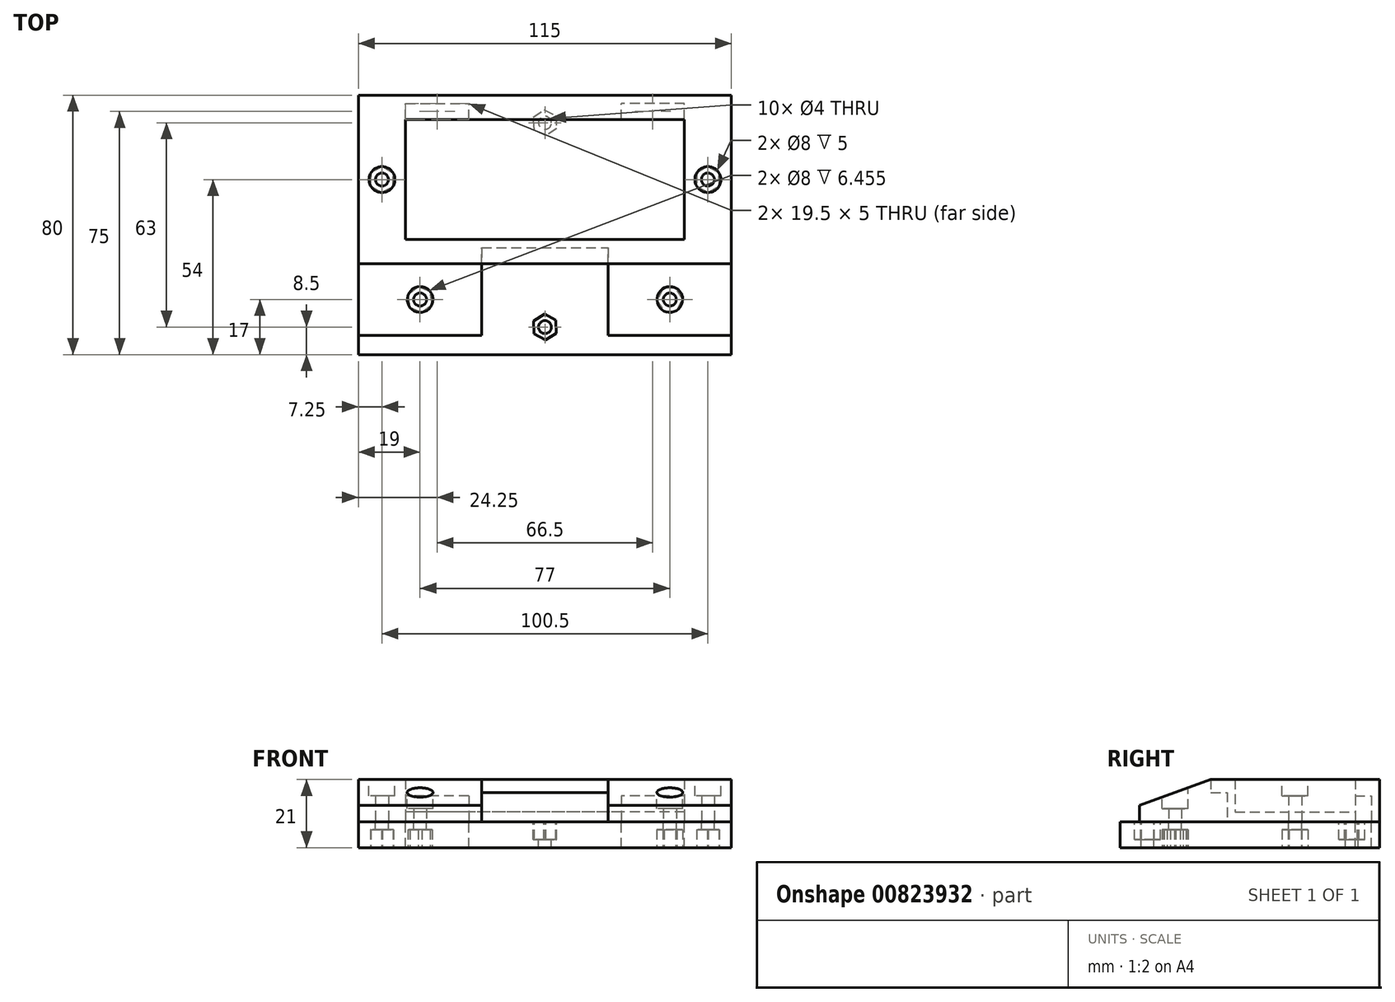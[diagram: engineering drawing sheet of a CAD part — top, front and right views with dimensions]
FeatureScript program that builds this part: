
annotation { "Feature Type Name" : "Feature", "Feature Type Description" : "" }
export const myFeature = defineFeature(function(context is Context, id is Id, definition is map)
    precondition{}
    {
        {
            var Q0;
            Q0=qCreatedBy(makeId("Top.planeOp"),FACE);
            var sketch = newSketch(context, id + "F0", { "sketchPlane" : qUnion([Q0])});
            skLineSegment(sketch, "E0.bottom", {"start": v(1460.5, -1028.53) * mm, "end": v(-1460.5, -1028.53) * mm});
            skLineSegment(sketch, "E0.top", {"start": v(1460.5, 1028.53) * mm, "end": v(-1460.5, 1028.53) * mm});
            skLineSegment(sketch, "E0.left", {"start": v(1460.5, -1028.53) * mm, "end": v(1460.5, 1028.53) * mm});
            skLineSegment(sketch, "E0.right", {"start": v(-1460.5, -1028.53) * mm, "end": v(-1460.5, 1028.53) * mm});
            skPoint(sketch, "E0.middle", {"position": v(0, 0) * mm});
            skLineSegment(sketch, "E1.bottom", {"start": v(57.5, -26) * mm, "end": v(-57.5, -26) * mm});
            skLineSegment(sketch, "E1.top", {"start": v(57.5, 26) * mm, "end": v(-57.5, 26) * mm});
            skLineSegment(sketch, "E1.left", {"start": v(57.5, -26) * mm, "end": v(57.5, 26) * mm});
            skLineSegment(sketch, "E1.right", {"start": v(-57.5, -26) * mm, "end": v(-57.5, 26) * mm});
            skLineSegment(sketch, "E2.bottom", {"start": v(43, -18.5) * mm, "end": v(-43, -18.5) * mm});
            skLineSegment(sketch, "E2.top", {"start": v(43, 18.5) * mm, "end": v(-43, 18.5) * mm});
            skLineSegment(sketch, "E2.left", {"start": v(43, -18.5) * mm, "end": v(43, 18.5) * mm});
            skLineSegment(sketch, "E2.right", {"start": v(-43, -18.5) * mm, "end": v(-43, 18.5) * mm});
            skLineSegment(sketch, "E3.bottom", {"start": v(-57.5, -26) * mm, "end": v(-19.5, -26) * mm});
            skLineSegment(sketch, "E3.top", {"start": v(-57.5, -48) * mm, "end": v(-19.5, -48) * mm});
            skLineSegment(sketch, "E3.left", {"start": v(-57.5, -26) * mm, "end": v(-57.5, -48) * mm});
            skLineSegment(sketch, "E3.right", {"start": v(-19.5, -26) * mm, "end": v(-19.5, -48) * mm});
            skLineSegment(sketch, "E4.bottom", {"start": v(57.5, -26) * mm, "end": v(19.5, -26) * mm});
            skLineSegment(sketch, "E4.top", {"start": v(57.5, -48) * mm, "end": v(19.5, -48) * mm});
            skLineSegment(sketch, "E4.left", {"start": v(57.5, -26) * mm, "end": v(57.5, -48) * mm});
            skLineSegment(sketch, "E4.right", {"start": v(19.5, -26) * mm, "end": v(19.5, -48) * mm});
            skLineSegment(sketch, "E5.bottom", {"start": v(-43, 18.5) * mm, "end": v(-23.5, 18.5) * mm});
            skLineSegment(sketch, "E5.top", {"start": v(-43, 23.5) * mm, "end": v(-23.5, 23.5) * mm});
            skLineSegment(sketch, "E5.left", {"start": v(-43, 18.5) * mm, "end": v(-43, 23.5) * mm});
            skLineSegment(sketch, "E5.right", {"start": v(-23.5, 18.5) * mm, "end": v(-23.5, 23.5) * mm});
            skLineSegment(sketch, "E6.bottom", {"start": v(43, 18.5) * mm, "end": v(23.5, 18.5) * mm});
            skLineSegment(sketch, "E6.top", {"start": v(43, 23.5) * mm, "end": v(23.5, 23.5) * mm});
            skLineSegment(sketch, "E6.left", {"start": v(43, 18.5) * mm, "end": v(43, 23.5) * mm});
            skLineSegment(sketch, "E6.right", {"start": v(23.5, 18.5) * mm, "end": v(23.5, 23.5) * mm});
            skLineSegment(sketch, "E7.bottom", {"start": v(-19.5, -26) * mm, "end": v(19.5, -26) * mm});
            skLineSegment(sketch, "E7.top", {"start": v(-19.5, -21) * mm, "end": v(19.5, -21) * mm});
            skLineSegment(sketch, "E7.left", {"start": v(-19.5, -26) * mm, "end": v(-19.5, -21) * mm});
            skLineSegment(sketch, "E7.right", {"start": v(19.5, -26) * mm, "end": v(19.5, -21) * mm});
            skLineSegment(sketch, "E8", {"start": v(-57.5, -48) * mm, "end": v(-19.5, -26) * mm, "construction": true});
            skLineSegment(sketch, "E9", {"start": v(-57.5, -26) * mm, "end": v(-19.5, -48) * mm, "construction": true});
            skLineSegment(sketch, "E10", {"start": v(19.5, -26) * mm, "end": v(57.5, -48) * mm, "construction": true});
            skLineSegment(sketch, "E11", {"start": v(57.5, -26) * mm, "end": v(19.5, -48) * mm, "construction": true});
            skCircle(sketch, "E12", {"center": v(-38.5, -37) * mm, "radius": 4 * mm});
            skCircle(sketch, "E13", {"center": v(38.5, -37) * mm, "radius": 4 * mm});
            skCircle(sketch, "E14", {"center": v(-38.5, -37) * mm, "radius": 2 * mm});
            skCircle(sketch, "E15", {"center": v(38.5, -37) * mm, "radius": 2 * mm});
            skLineSegment(sketch, "E16", {"start": v(-57.5, 0) * mm, "end": v(-43, 0) * mm, "construction": true});
            skLineSegment(sketch, "E17", {"start": v(-43, 0) * mm, "end": v(43, 0) * mm, "construction": true});
            skLineSegment(sketch, "E18", {"start": v(43, 0) * mm, "end": v(57.5, 0) * mm, "construction": true});
            skPoint(sketch, "E19", {"position": v(-50.25, 0) * mm});
            skPoint(sketch, "E20", {"position": v(50.25, 0) * mm});
            skCircle(sketch, "E21", {"center": v(-50.25, 0) * mm, "radius": 4 * mm});
            skCircle(sketch, "E22", {"center": v(50.25, 0) * mm, "radius": 4 * mm});
            skCircle(sketch, "E23", {"center": v(50.25, 0) * mm, "radius": 2 * mm});
            skCircle(sketch, "E24", {"center": v(-50.25, 0) * mm, "radius": 2 * mm});
            skSolve(sketch);
        }
        {
            var Q0;
            Q0=makeQuery(id+"F0.imprint","IMPRINT",FACE,{"disambiguationData":[TD([[makeQuery(id+"F0.imprint","IMPRINT",EDGE,{"derivedFrom":sQuery(id+"F0.wireOp",EDGE,"E1.top")}),1.0]])]});
            var Q1;
            Q1=makeQuery(id+"F0.imprint","IMPRINT",FACE,{"disambiguationData":[TD([[makeQuery(id+"F0.imprint","IMPRINT",EDGE,{"derivedFrom":sQuery(id+"F0.wireOp",EDGE,"E21")}),1.0]])]});
            var Q2;
            Q2=makeQuery(id+"F0.imprint","IMPRINT",FACE,{"disambiguationData":[TD([[makeQuery(id+"F0.imprint","IMPRINT",EDGE,{"derivedFrom":sQuery(id+"F0.wireOp",EDGE,"E22")}),1.0]])]});
            var Q3;
            Q3=makeQuery(id+"F0.imprint","IMPRINT",FACE,{"disambiguationData":[TD([[makeQuery(id+"F0.imprint","IMPRINT",EDGE,{"derivedFrom":sQuery(id+"F0.wireOp",EDGE,"E5.top")}),-1.0]])]});
            var Q4;
            Q4=makeQuery(id+"F0.imprint","IMPRINT",FACE,{"disambiguationData":[TD([[makeQuery(id+"F0.imprint","IMPRINT",EDGE,{"derivedFrom":sQuery(id+"F0.wireOp",EDGE,"E6.top")}),1.0]])]});
            var Q5;
            Q5=makeQuery(id+"F0.imprint","IMPRINT",FACE,{"disambiguationData":[TD([[makeQuery(id+"F0.imprint","IMPRINT",EDGE,{"derivedFrom":sQuery(id+"F0.wireOp",EDGE,"E7.top")}),-1.0]])]});
            extrude(context, id + "F1", {"entities" : qUnion([Q0, Q1, Q2, Q3, Q4, Q5]), "depth" : 13 * mm, "offsetDistance" : 25 * mm});
        }
        {
            var Q0;
            Q0=makeQuery(id+"F0.imprint","IMPRINT",FACE,{"disambiguationData":[TD([[makeQuery(id+"F0.imprint","IMPRINT",EDGE,{"derivedFrom":sQuery(id+"F0.wireOp",EDGE,"E2.bottom")}),-1.0]])]});
            extrude(context, id + "F2", {"entities" : qUnion([Q0]), "operationType" : NewBodyOperationType.ADD, "depth" : 3 * mm, "offsetDistance" : 25 * mm});
        }
        {
            var Q0;
            Q0=makeQuery(id+"F0.imprint","IMPRINT",FACE,{"disambiguationData":[TD([[makeQuery(id+"F0.imprint","IMPRINT",EDGE,{"derivedFrom":sQuery(id+"F0.wireOp",EDGE,"E5.top")}),-1.0]])]});
            var Q1;
            Q1=makeQuery(id+"F0.imprint","IMPRINT",FACE,{"disambiguationData":[TD([[makeQuery(id+"F0.imprint","IMPRINT",EDGE,{"derivedFrom":sQuery(id+"F0.wireOp",EDGE,"E6.top")}),1.0]])]});
            extrude(context, id + "F3", {"entities" : qUnion([Q0, Q1]), "operationType" : NewBodyOperationType.REMOVE, "oppositeDirection" : true, "depth" : -8 * mm, "offsetDistance" : 25 * mm});
        }
        {
            var Q0;
            Q0=makeQuery(id+"F0.imprint","IMPRINT",FACE,{"disambiguationData":[TD([[makeQuery(id+"F0.imprint","IMPRINT",EDGE,{"derivedFrom":sQuery(id+"F0.wireOp",EDGE,"E3.top")}),1.0]])]});
            var Q1;
            Q1=makeQuery(id+"F0.imprint","IMPRINT",FACE,{"disambiguationData":[TD([[makeQuery(id+"F0.imprint","IMPRINT",EDGE,{"derivedFrom":sQuery(id+"F0.wireOp",EDGE,"E12")}),1.0]])]});
            var Q2;
            Q2=makeQuery(id+"F0.imprint","IMPRINT",FACE,{"disambiguationData":[TD([[makeQuery(id+"F0.imprint","IMPRINT",EDGE,{"derivedFrom":sQuery(id+"F0.wireOp",EDGE,"E4.top")}),-1.0]])]});
            var Q3;
            Q3=makeQuery(id+"F0.imprint","IMPRINT",FACE,{"disambiguationData":[TD([[makeQuery(id+"F0.imprint","IMPRINT",EDGE,{"derivedFrom":sQuery(id+"F0.wireOp",EDGE,"E13")}),1.0]])]});
            extrude(context, id + "F4", {"entities" : qUnion([Q0, Q1, Q2, Q3]), "operationType" : NewBodyOperationType.ADD, "depth" : 5 * mm, "offsetDistance" : 25 * mm});
        }
        {
            var Q0;
            Q0=makeQuery(id+"F0.imprint","IMPRINT",FACE,{"disambiguationData":[TD([[makeQuery(id+"F0.imprint","IMPRINT",EDGE,{"derivedFrom":sQuery(id+"F0.wireOp",EDGE,"E7.top")}),-1.0]])]});
            extrude(context, id + "F5", {"entities" : qUnion([Q0]), "operationType" : NewBodyOperationType.REMOVE, "oppositeDirection" : true, "depth" : -9 * mm, "offsetDistance" : 25 * mm});
        }
        {
            var Q0;
            Q0=makeQuery(id+"F4.boolean.opBoolean","MERGE",FACE,{"derivedFrom":[makeQuery(id+"F1.opExtrude","SWEPT_FACE",FACE,{"disambiguationData":[OSD([sQuery(id+"F0.wireOp",EDGE,"E1.left")])]}),makeQuery(id+"F4.opExtrude","SWEPT_FACE",FACE,{"disambiguationData":[OSD([sQuery(id+"F0.wireOp",EDGE,"E4.left")])]})]});
            var sketch = newSketch(context, id + "F6", { "sketchPlane" : qUnion([Q0])});
            skLineSegment(sketch, "E25", {"start": v(-26, 13) * mm, "end": v(-48, 5) * mm});
            skSolve(sketch);
        }
        {
            var Q0;
            Q0=makeQuery(id+"F6.imprint","IMPRINT",FACE,{"disambiguationData":[TD([[makeQuery(id+"F6.imprint","IMPRINT",EDGE,{"derivedFrom":sQuery(id+"F6.wireOp",EDGE,"E25")}),1.0]])]});
            extrude(context, id + "F7", {"entities" : qUnion([Q0]), "operationType" : NewBodyOperationType.ADD, "oppositeDirection" : true, "depth" : 38 * mm, "offsetDistance" : 25 * mm});
        }
        {
            var Q0;
            Q0=makeQuery(id+"F4.boolean.opBoolean","MERGE",FACE,{"derivedFrom":[makeQuery(id+"F1.opExtrude","SWEPT_FACE",FACE,{"disambiguationData":[OSD([sQuery(id+"F0.wireOp",EDGE,"E1.right")])]}),makeQuery(id+"F4.opExtrude","SWEPT_FACE",FACE,{"disambiguationData":[OSD([sQuery(id+"F0.wireOp",EDGE,"E3.left")])]})]});
            var sketch = newSketch(context, id + "F8", { "sketchPlane" : qUnion([Q0])});
            skLineSegment(sketch, "E26", {"start": v(26, 13) * mm, "end": v(48, 5) * mm});
            skSolve(sketch);
        }
        {
            var Q0;
            Q0=makeQuery(id+"F8.imprint","IMPRINT",FACE,{"disambiguationData":[TD([[makeQuery(id+"F8.imprint","IMPRINT",EDGE,{"derivedFrom":sQuery(id+"F8.wireOp",EDGE,"E26")}),-1.0]])]});
            extrude(context, id + "F9", {"entities" : qUnion([Q0]), "operationType" : NewBodyOperationType.ADD, "oppositeDirection" : true, "depth" : 38 * mm, "offsetDistance" : 25 * mm});
        }
        {
            var Q0;
            Q0=makeQuery(id+"F1.opExtrude","CAP_FACE",FACE,{"disambiguationData":[OSD([sQuery(id+"F0.wireOp",EDGE,"E1.bottom"),sQuery(id+"F0.wireOp",EDGE,"E1.top"),sQuery(id+"F0.wireOp",EDGE,"E1.left"),sQuery(id+"F0.wireOp",EDGE,"E1.right"),sQuery(id+"F0.wireOp",EDGE,"E2.bottom"),sQuery(id+"F0.wireOp",EDGE,"E2.top"),sQuery(id+"F0.wireOp",EDGE,"E2.left"),sQuery(id+"F0.wireOp",EDGE,"E2.right"),sQuery(id+"F0.wireOp",EDGE,"E23"),sQuery(id+"F0.wireOp",EDGE,"E24")])],"isStart":false});
            var sketch = newSketch(context, id + "F10", { "sketchPlane" : qUnion([Q0])});
            skCircle(sketch, "E27", {"center": v(-50.25, 0) * mm, "radius": 4 * mm});
            skCircle(sketch, "E28", {"center": v(50.25, 0) * mm, "radius": 4 * mm});
            skCircle(sketch, "E29", {"center": v(38.5, -37) * mm, "radius": 4 * mm});
            skCircle(sketch, "E30", {"center": v(-38.5, -37) * mm, "radius": 4 * mm});
            skSolve(sketch);
        }
        {
            var Q0;
            Q0=makeQuery(id+"F10.imprint","IMPRINT",FACE,{"disambiguationData":[TD([[makeQuery(id+"F10.imprint","IMPRINT",EDGE,{"derivedFrom":sQuery(id+"F10.wireOp",EDGE,"E27")}),1.0]])]});
            var Q1;
            Q1=makeQuery(id+"F10.imprint","IMPRINT",FACE,{"disambiguationData":[TD([[makeQuery(id+"F10.imprint","IMPRINT",EDGE,{"derivedFrom":sQuery(id+"F10.wireOp",EDGE,"E28")}),1.0]])]});
            extrude(context, id + "F11", {"entities" : qUnion([Q0, Q1]), "operationType" : NewBodyOperationType.REMOVE, "oppositeDirection" : true, "depth" : 5 * mm, "offsetDistance" : 25 * mm});
        }
        {
            var Q0;
            Q0=makeQuery(id+"F0.imprint","IMPRINT",FACE,{"disambiguationData":[TD([[makeQuery(id+"F0.imprint","IMPRINT",EDGE,{"derivedFrom":sQuery(id+"F0.wireOp",EDGE,"E15")}),1.0]])]});
            var Q1;
            Q1=makeQuery(id+"F0.imprint","IMPRINT",FACE,{"disambiguationData":[TD([[makeQuery(id+"F0.imprint","IMPRINT",EDGE,{"derivedFrom":sQuery(id+"F0.wireOp",EDGE,"E14")}),1.0]])]});
            extrude(context, id + "F12", {"entities" : qUnion([Q0, Q1]), "operationType" : NewBodyOperationType.REMOVE, "depth" : 25 * mm, "offsetDistance" : 25 * mm});
        }
        {
            var Q0;
            Q0=makeQuery(id+"F10.imprint","IMPRINT",FACE,{"disambiguationData":[TD([[makeQuery(id+"F10.imprint","IMPRINT",EDGE,{"derivedFrom":sQuery(id+"F10.wireOp",EDGE,"E30")}),1.0]])]});
            var Q1;
            Q1=makeQuery(id+"F10.imprint","IMPRINT",FACE,{"disambiguationData":[TD([[makeQuery(id+"F10.imprint","IMPRINT",EDGE,{"derivedFrom":sQuery(id+"F10.wireOp",EDGE,"E29")}),1.0]])]});
            extrude(context, id + "F13", {"entities" : qUnion([Q0, Q1]), "operationType" : NewBodyOperationType.REMOVE, "oppositeDirection" : true, "depth" : 9 * mm, "offsetDistance" : 25 * mm});
        }
        {
            var Q0;
            {var subQ0=sQuery(id+"F0.wireOp",EDGE,"E1.bottom");var subQ1=sQuery(id+"F0.wireOp",EDGE,"E2.right");var subQ2=sQuery(id+"F0.wireOp",EDGE,"E2.left");var subQ3=sQuery(id+"F0.wireOp",EDGE,"E2.top");var subQ4=sQuery(id+"F0.wireOp",EDGE,"E2.bottom");Q0=makeQuery(id+"F4.boolean.opBoolean","MERGE",FACE,{"derivedFrom":[makeQuery(id+"F2.boolean.opBoolean","MERGE",FACE,{"derivedFrom":[makeQuery(id+"F1.opExtrude","CAP_FACE",FACE,{"disambiguationData":[OSD([subQ0,sQuery(id+"F0.wireOp",EDGE,"E1.top"),sQuery(id+"F0.wireOp",EDGE,"E1.left"),sQuery(id+"F0.wireOp",EDGE,"E1.right"),subQ4,subQ3,subQ2,subQ1,sQuery(id+"F0.wireOp",EDGE,"E23"),sQuery(id+"F0.wireOp",EDGE,"E24")])],"isStart":true}),makeQuery(id+"F2.opExtrude","CAP_FACE",FACE,{"disambiguationData":[OSD([subQ4,subQ3,subQ2,subQ1])],"isStart":true})]}),makeQuery(id+"F4.opExtrude","CAP_FACE",FACE,{"disambiguationData":[OSD([subQ0,sQuery(id+"F0.wireOp",EDGE,"E3.top"),sQuery(id+"F0.wireOp",EDGE,"E3.left"),sQuery(id+"F0.wireOp",EDGE,"E3.right"),sQuery(id+"F0.wireOp",EDGE,"E14")])],"isStart":true}),makeQuery(id+"F4.opExtrude","CAP_FACE",FACE,{"disambiguationData":[OSD([subQ0,sQuery(id+"F0.wireOp",EDGE,"E4.top"),sQuery(id+"F0.wireOp",EDGE,"E4.left"),sQuery(id+"F0.wireOp",EDGE,"E4.right"),sQuery(id+"F0.wireOp",EDGE,"E15")])],"isStart":true})]});}
            var sketch = newSketch(context, id + "F14", { "sketchPlane" : qUnion([Q0])});
            skLineSegment(sketch, "E31.bottom", {"start": v(57.5, -26) * mm, "end": v(-57.5, -26) * mm});
            skLineSegment(sketch, "E31.top", {"start": v(57.5, 54) * mm, "end": v(-57.5, 54) * mm});
            skLineSegment(sketch, "E31.left", {"start": v(57.5, -26) * mm, "end": v(57.5, 54) * mm});
            skLineSegment(sketch, "E31.right", {"start": v(-57.5, -26) * mm, "end": v(-57.5, 54) * mm});
            skCircle(sketch, "E32", {"center": v(50.25, 0) * mm, "radius": 2 * mm});
            skCircle(sketch, "E33", {"center": v(-50.25, 0) * mm, "radius": 2 * mm});
            skCircle(sketch, "E34", {"center": v(-38.5, 37) * mm, "radius": 2 * mm});
            skCircle(sketch, "E35", {"center": v(38.5, 37) * mm, "radius": 2 * mm});
            skCircle(sketch, "E36", {"center": v(0, -17.5) * mm, "radius": 2 * mm});
            skCircle(sketch, "E37", {"center": v(0, 45.5) * mm, "radius": 2 * mm});
            skSolve(sketch);
        }
        {
            var Q0;
            {var subQ2=sQuery(id+"F14.wireOp",EDGE,"E31.top");Q0=makeQuery(id+"F14.imprint","IMPRINT",FACE,{"disambiguationData":[TD([[makeQuery(id+"F14.imprint","IMPRINT",EDGE,{"derivedFrom":subQ2}),1.0]])]});}
            var Q1;
            {var subQ0=sQuery(id+"F14.wireOp",EDGE,"E31.bottom");Q1=makeQuery(id+"F14.imprint","IMPRINT",FACE,{"disambiguationData":[TD([[makeQuery(id+"F14.imprint","IMPRINT",EDGE,{"derivedFrom":subQ0}),-1.0]])]});}
            var Q2;
            Q2=makeQuery(id+"F14.imprint","IMPRINT",FACE,{"disambiguationData":[TD([[makeQuery(id+"F14.imprint","IMPRINT",EDGE,{"derivedFrom":makeQuery(id+"F3.boolean.opBoolean","COPY",EDGE,{"derivedFrom":makeQuery(id+"F3.opExtrude","CAP_EDGE",EDGE,{"disambiguationData":[OSD([sQuery(id+"F0.wireOp",EDGE,"E6.top")])],"isStart":true})})}),-1.0]])]});
            var Q3;
            Q3=makeQuery(id+"F14.imprint","IMPRINT",FACE,{"disambiguationData":[TD([[makeQuery(id+"F14.imprint","IMPRINT",EDGE,{"derivedFrom":makeQuery(id+"F3.boolean.opBoolean","COPY",EDGE,{"derivedFrom":makeQuery(id+"F3.opExtrude","CAP_EDGE",EDGE,{"disambiguationData":[OSD([sQuery(id+"F0.wireOp",EDGE,"E5.top")])],"isStart":true})})}),1.0]])]});
            extrude(context, id + "F15", {"entities" : qUnion([Q0, Q1, Q2, Q3]), "depth" : 8 * mm, "offsetDistance" : 25 * mm});
        }
        {
            var Q0;
            Q0=makeQuery(id+"F15.opExtrude","CAP_FACE",FACE,{"disambiguationData":[OSD([sQuery(id+"F14.wireOp",EDGE,"E31.bottom"),sQuery(id+"F14.wireOp",EDGE,"E31.top"),sQuery(id+"F14.wireOp",EDGE,"E31.left"),sQuery(id+"F14.wireOp",EDGE,"E31.right"),sQuery(id+"F14.wireOp",EDGE,"E32"),sQuery(id+"F14.wireOp",EDGE,"E33"),sQuery(id+"F14.wireOp",EDGE,"E34"),sQuery(id+"F14.wireOp",EDGE,"E35"),sQuery(id+"F14.wireOp",EDGE,"E36"),sQuery(id+"F14.wireOp",EDGE,"E37")])],"isStart":true});
            var sketch = newSketch(context, id + "F16", { "sketchPlane" : qUnion([Q0])});
            skCircle(sketch, "E38.cCircle", {"center": v(0, 17.5) * mm, "radius": 4 * mm, "construction": true});
            skLineSegment(sketch, "E38.0", {"start": v(3.6, 15.76) * mm, "end": v(0.29, 13.51) * mm});
            skLineSegment(sketch, "E38.1", {"start": v(0.29, 13.51) * mm, "end": v(-3.31, 15.26) * mm});
            skLineSegment(sketch, "E38.2", {"start": v(-3.31, 15.26) * mm, "end": v(-3.6, 19.24) * mm});
            skLineSegment(sketch, "E38.3", {"start": v(-3.6, 19.24) * mm, "end": v(-0.29, 21.49) * mm});
            skLineSegment(sketch, "E38.4", {"start": v(-0.29, 21.49) * mm, "end": v(3.31, 19.74) * mm});
            skLineSegment(sketch, "E38.5", {"start": v(3.31, 19.74) * mm, "end": v(3.6, 15.76) * mm});
            skCircle(sketch, "E39.cCircle", {"center": v(0, -45.5) * mm, "radius": 4 * mm, "construction": true});
            skLineSegment(sketch, "E39.0", {"start": v(3.52, -47.4) * mm, "end": v(0.12, -49.5) * mm});
            skLineSegment(sketch, "E39.1", {"start": v(0.12, -49.5) * mm, "end": v(-3.4, -47.6) * mm});
            skLineSegment(sketch, "E39.2", {"start": v(-3.4, -47.6) * mm, "end": v(-3.52, -43.6) * mm});
            skLineSegment(sketch, "E39.3", {"start": v(-3.52, -43.6) * mm, "end": v(-0.12, -41.5) * mm});
            skLineSegment(sketch, "E39.4", {"start": v(-0.12, -41.5) * mm, "end": v(3.4, -43.4) * mm});
            skLineSegment(sketch, "E39.5", {"start": v(3.4, -43.4) * mm, "end": v(3.52, -47.4) * mm});
            skSolve(sketch);
        }
        {
            var Q0;
            Q0=makeQuery(id+"F16.imprint","IMPRINT",FACE,{"disambiguationData":[TD([[makeQuery(id+"F16.imprint","IMPRINT",EDGE,{"derivedFrom":sQuery(id+"F16.wireOp",EDGE,"E38.0")}),-1.0]])]});
            var Q1;
            Q1=makeQuery(id+"F16.imprint","IMPRINT",FACE,{"disambiguationData":[TD([[makeQuery(id+"F16.imprint","IMPRINT",EDGE,{"derivedFrom":sQuery(id+"F16.wireOp",EDGE,"E39.0")}),-1.0]])]});
            extrude(context, id + "F17", {"entities" : qUnion([Q0, Q1]), "operationType" : NewBodyOperationType.REMOVE, "oppositeDirection" : true, "depth" : 5.5 * mm, "offsetDistance" : 25 * mm});
        }
        {
            var Q0;
            Q0=makeQuery(id+"F15.opExtrude","CAP_FACE",FACE,{"disambiguationData":[OSD([sQuery(id+"F14.wireOp",EDGE,"E31.bottom"),sQuery(id+"F14.wireOp",EDGE,"E31.top"),sQuery(id+"F14.wireOp",EDGE,"E31.left"),sQuery(id+"F14.wireOp",EDGE,"E31.right"),sQuery(id+"F14.wireOp",EDGE,"E32"),sQuery(id+"F14.wireOp",EDGE,"E33"),sQuery(id+"F14.wireOp",EDGE,"E34"),sQuery(id+"F14.wireOp",EDGE,"E35"),sQuery(id+"F14.wireOp",EDGE,"E36"),sQuery(id+"F14.wireOp",EDGE,"E37")])],"isStart":false});
            var sketch = newSketch(context, id + "F18", { "sketchPlane" : qUnion([Q0])});
            skCircle(sketch, "E40.cCircle", {"center": v(-38.5, 37) * mm, "radius": 4 * mm, "construction": true});
            skLineSegment(sketch, "E40.0", {"start": v(-35.33, 34.56) * mm, "end": v(-39.02, 33.03) * mm});
            skLineSegment(sketch, "E40.1", {"start": v(-39.02, 33.03) * mm, "end": v(-42.2, 35.47) * mm});
            skLineSegment(sketch, "E40.2", {"start": v(-42.2, 35.47) * mm, "end": v(-41.67, 39.44) * mm});
            skLineSegment(sketch, "E40.3", {"start": v(-41.67, 39.44) * mm, "end": v(-37.98, 40.97) * mm});
            skLineSegment(sketch, "E40.4", {"start": v(-37.98, 40.97) * mm, "end": v(-34.8, 38.53) * mm});
            skLineSegment(sketch, "E40.5", {"start": v(-34.8, 38.53) * mm, "end": v(-35.33, 34.56) * mm});
            skCircle(sketch, "E41.cCircle", {"center": v(38.5, 37) * mm, "radius": 4 * mm, "construction": true});
            skLineSegment(sketch, "E41.0", {"start": v(36.3, 33.66) * mm, "end": v(34.5, 37.23) * mm});
            skLineSegment(sketch, "E41.1", {"start": v(34.5, 37.23) * mm, "end": v(36.7, 40.57) * mm});
            skLineSegment(sketch, "E41.2", {"start": v(36.7, 40.57) * mm, "end": v(40.7, 40.34) * mm});
            skLineSegment(sketch, "E41.3", {"start": v(40.7, 40.34) * mm, "end": v(42.5, 36.77) * mm});
            skLineSegment(sketch, "E41.4", {"start": v(42.5, 36.77) * mm, "end": v(40.3, 33.43) * mm});
            skLineSegment(sketch, "E41.5", {"start": v(40.3, 33.43) * mm, "end": v(36.3, 33.66) * mm});
            skCircle(sketch, "E42.cCircle", {"center": v(-50.25, 0) * mm, "radius": 4 * mm, "construction": true});
            skLineSegment(sketch, "E42.0", {"start": v(-46.73, -1.9) * mm, "end": v(-50.14, -4) * mm});
            skLineSegment(sketch, "E42.1", {"start": v(-50.14, -4) * mm, "end": v(-53.66, -2.1) * mm});
            skLineSegment(sketch, "E42.2", {"start": v(-53.66, -2.1) * mm, "end": v(-53.77, 1.9) * mm});
            skLineSegment(sketch, "E42.3", {"start": v(-53.77, 1.9) * mm, "end": v(-50.36, 4) * mm});
            skLineSegment(sketch, "E42.4", {"start": v(-50.36, 4) * mm, "end": v(-46.84, 2.1) * mm});
            skLineSegment(sketch, "E42.5", {"start": v(-46.84, 2.1) * mm, "end": v(-46.73, -1.9) * mm});
            skCircle(sketch, "E43.cCircle", {"center": v(50.25, 0) * mm, "radius": 4 * mm, "construction": true});
            skLineSegment(sketch, "E43.0", {"start": v(46.73, -1.9) * mm, "end": v(46.84, 2.1) * mm});
            skLineSegment(sketch, "E43.1", {"start": v(46.84, 2.1) * mm, "end": v(50.36, 4) * mm});
            skLineSegment(sketch, "E43.2", {"start": v(50.36, 4) * mm, "end": v(53.77, 1.9) * mm});
            skLineSegment(sketch, "E43.3", {"start": v(53.77, 1.9) * mm, "end": v(53.66, -2.1) * mm});
            skLineSegment(sketch, "E43.4", {"start": v(53.66, -2.1) * mm, "end": v(50.14, -4) * mm});
            skLineSegment(sketch, "E43.5", {"start": v(50.14, -4) * mm, "end": v(46.73, -1.9) * mm});
            skSolve(sketch);
        }
        {
            var Q0;
            Q0=makeQuery(id+"F18.imprint","IMPRINT",FACE,{"disambiguationData":[TD([[makeQuery(id+"F18.imprint","IMPRINT",EDGE,{"derivedFrom":sQuery(id+"F18.wireOp",EDGE,"E40.0")}),-1.0]])]});
            var Q1;
            Q1=makeQuery(id+"F18.imprint","IMPRINT",FACE,{"disambiguationData":[TD([[makeQuery(id+"F18.imprint","IMPRINT",EDGE,{"derivedFrom":sQuery(id+"F18.wireOp",EDGE,"E41.0")}),-1.0]])]});
            var Q2;
            Q2=makeQuery(id+"F18.imprint","IMPRINT",FACE,{"disambiguationData":[TD([[makeQuery(id+"F18.imprint","IMPRINT",EDGE,{"derivedFrom":sQuery(id+"F18.wireOp",EDGE,"E43.0")}),-1.0]])]});
            var Q3;
            Q3=makeQuery(id+"F18.imprint","IMPRINT",FACE,{"disambiguationData":[TD([[makeQuery(id+"F18.imprint","IMPRINT",EDGE,{"derivedFrom":sQuery(id+"F18.wireOp",EDGE,"E42.0")}),-1.0]])]});
            extrude(context, id + "F19", {"entities" : qUnion([Q0, Q1, Q2, Q3]), "operationType" : NewBodyOperationType.REMOVE, "oppositeDirection" : true, "depth" : 5.5 * mm, "offsetDistance" : 25 * mm});
        }
    });
